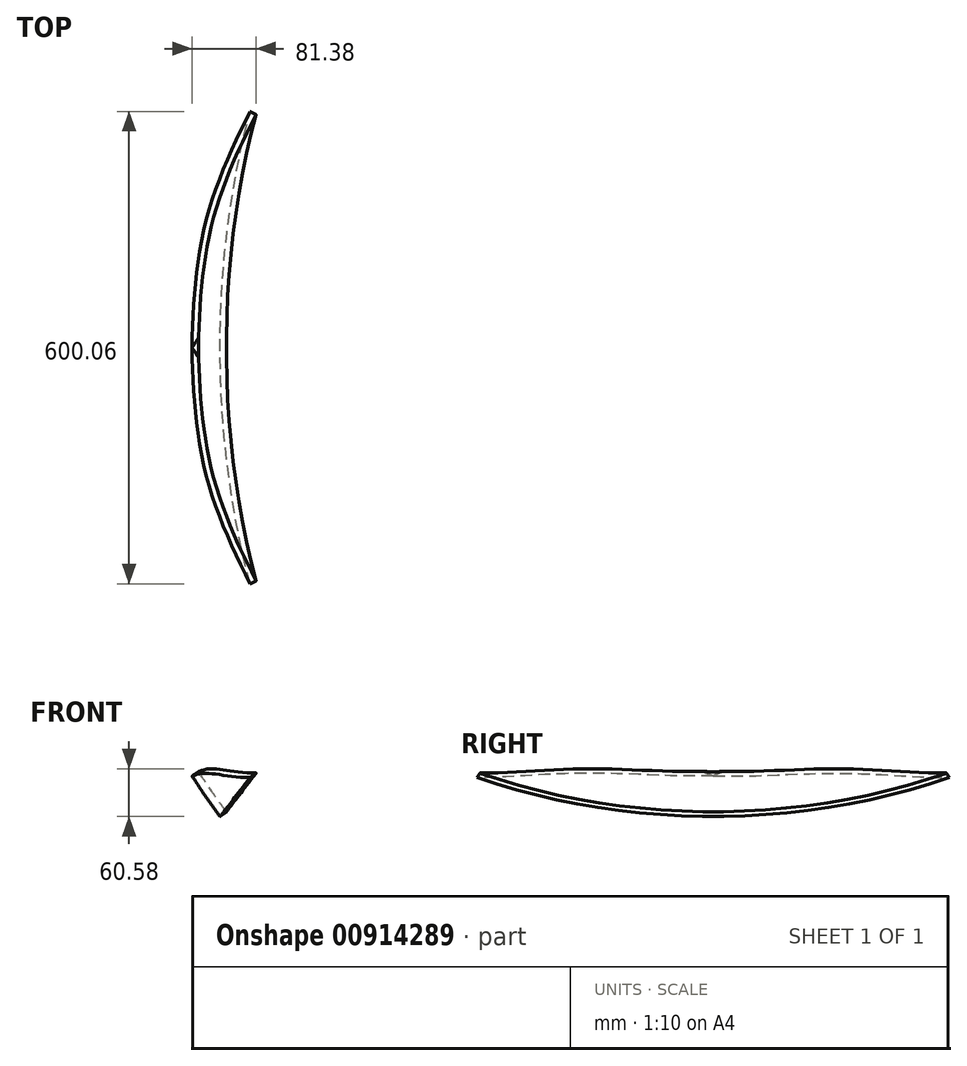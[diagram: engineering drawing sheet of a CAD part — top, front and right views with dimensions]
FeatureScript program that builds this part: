
annotation { "Feature Type Name" : "Feature", "Feature Type Description" : "" }
export const myFeature = defineFeature(function(context is Context, id is Id, definition is map)
    precondition{}
    {
        {
            var Q0;
            Q0=qCreatedBy(makeId("Front.planeOp"),FACE);
            var sketch = newSketch(context, id + "F0", { "sketchPlane" : qUnion([Q0])});
            skLineSegment(sketch, "E0", {"start": v(-634.43, -400) * mm, "end": v(-559, -400) * mm, "construction": true});
            skLineSegment(sketch, "E1", {"start": v(-559, -400) * mm, "end": v(-559, -500.02) * mm, "construction": true});
            skArc(sketch, "E2.trimOffspring", {"start": v(-634.43, -400) * mm, "mid": v(-617.16, -426.17) * mm, "end": v(-598.8, -451.59) * mm});
            skPoint(sketch, "E3.start.orphan", {"position": v(-750, 0) * mm});
            skPoint(sketch, "E4.orphan", {"position": v(0, -750) * mm});
            skLineSegment(sketch, "E5", {"start": v(-559, -500.02) * mm, "end": v(0, 0) * mm, "construction": true});
            skLineSegment(sketch, "E6", {"start": v(0, 0) * mm, "end": v(-634.43, -400) * mm, "construction": true});
            skPoint(sketch, "E7.end.orphan", {"position": v(-598.8, -451.59) * mm});
            skLineSegment(sketch, "E8", {"start": v(-598.8, -451.59) * mm, "end": v(-559, -400) * mm, "construction": true});
            skLineSegment(sketch, "E9", {"start": v(-559, -400) * mm, "end": v(-478.9, -489.54) * mm, "construction": true});
            skLineSegment(sketch, "E10", {"start": v(-478.9, -489.54) * mm, "end": v(-509.3, -455.56) * mm, "construction": true});
            skLineSegment(sketch, "E11", {"start": v(-559, -400) * mm, "end": v(-621.65, -329.96) * mm, "construction": true});
            skLineSegment(sketch, "E12", {"start": v(0, 0) * mm, "end": v(-559, -400) * mm, "construction": true});
            skArc(sketch, "E13", {"start": v(0, 26.26) * mm, "mid": v(-23.36, 12) * mm, "end": v(-21.36, -15.28) * mm, "construction": true});
            skLineSegment(sketch, "E14", {"start": v(0, 0) * mm, "end": v(0, 26.26) * mm, "construction": true});
            skLineSegment(sketch, "E15", {"start": v(-634.43, -400) * mm, "end": v(-625.97, -394.67) * mm});
            skLineSegment(sketch, "E16", {"start": v(-559, -500.02) * mm, "end": v(-551.55, -493.35) * mm});
            skArc(sketch, "E17", {"start": v(-625.97, -394.67) * mm, "mid": v(-608.93, -420.48) * mm, "end": v(-590.82, -445.57) * mm});
            skLineSegment(sketch, "E18", {"start": v(-598.8, -451.59) * mm, "end": v(-590.82, -445.57) * mm});
            skSolve(sketch);
        }
        {
            var Q0;
            Q0=sQuery(id+"F0.wireOp",EDGE,"E8");
            cPlane(context, id + "F1", {"entities" : qUnion([Q0]), "cplaneType" : CPlaneType.LINE_ANGLE, "offset" : 25 * mm, "angle" : 0 * degree, "width" : 150 * mm, "height" : 150 * mm});
        }
        {
            var Q0;
            Q0=qCreatedBy(id+"F1.planeOp",FACE);
            var sketch = newSketch(context, id + "F2", { "sketchPlane" : qUnion([Q0])});
            skArc(sketch, "E19", {"start": v(0, -723.34) * mm, "mid": v(153.25, -707.51) * mm, "end": v(300.03, -660.71) * mm});
            skSolve(sketch);
        }
        {
            var Q0;
            Q0=sQuery(id+"F0.wireOp",VERTEX,"E0.start");
            var Q1;
            Q1=sQuery(id+"F0.wireOp",VERTEX,"E7.end.orphan");
            var Q2;
            Q2=sQuery(id+"F2.wireOp",VERTEX,"E19.end");
            cPlane(context, id + "F3", {"entities" : qUnion([Q0, Q1, Q2]), "cplaneType" : CPlaneType.THREE_POINT, "offset" : 25 * mm, "width" : 150 * mm, "height" : 150 * mm});
        }
        {
            var Q0;
            Q0=qCreatedBy(id+"F3.planeOp",FACE);
            var sketch = newSketch(context, id + "F4", { "sketchPlane" : qUnion([Q0])});
            skFitSpline(sketch, "E20", {"points": [v(146.13, 31.35) * mm, v(-17.39, 23.69) * mm, v(-159.77, -12.29) * mm], "startDerivative": vector(-323.62, -9.9) * mm, "endDerivative": vector(-282.1, -74.81) * mm});
            skLineSegment(sketch, "E21", {"start": v(-159.77, -12.29) * mm, "end": v(-190.52, 25.33) * mm});
            skLineSegment(sketch, "E22", {"start": v(-190.52, 25.33) * mm, "end": v(-149.4, 94.45) * mm});
            skLineSegment(sketch, "E23", {"start": v(-149.4, 94.45) * mm, "end": v(148.54, 94.45) * mm});
            skLineSegment(sketch, "E24", {"start": v(148.54, 94.45) * mm, "end": v(146.13, 31.35) * mm});
            skSolve(sketch);
        }
        {
            var Q0;
            Q0=makeQuery(id+"F0.imprint","IMPRINT",FACE,{"disambiguationData":[TD([[makeQuery(id+"F0.imprint","IMPRINT",EDGE,{"derivedFrom":sQuery(id+"F0.wireOp",EDGE,"E2.trimOffspring")}),1.0]])]});
            var Q1;
            Q1=sQuery(id+"F2.wireOp",EDGE,"E19");
            sweep(context, id + "F5", {"profiles" : qUnion([Q0]), "path" : qUnion([Q1])});
        }
        {
            var Q0;
            Q0 = qSketchRegion(id + "F4", true);
            extrude(context, id + "F6", {"entities" : qUnion([Q0]), "operationType" : NewBodyOperationType.REMOVE, "endBound" : BoundingType.SYMMETRIC, "oppositeDirection" : true, "depth" : 38 * mm, "offsetDistance" : 25 * mm});
        }
        {
            var Q0;
            Q0=makeQuery(id+"F5.opSweep","SWEPT_BODY",BODY,{"disambiguationData":[OSD([sQuery(id+"F0.wireOp",EDGE,"E2.trimOffspring"),sQuery(id+"F0.wireOp",EDGE,"E15"),sQuery(id+"F0.wireOp",EDGE,"E17"),sQuery(id+"F0.wireOp",EDGE,"E18"),sQuery(id+"F2.wireOp",EDGE,"E19")])]});
            var Q1;
            Q1=makeQuery(id+"F5.opSweep","CAP_FACE",FACE,{"disambiguationData":[OSD([sQuery(id+"F0.wireOp",EDGE,"E2.trimOffspring"),sQuery(id+"F0.wireOp",EDGE,"E15"),sQuery(id+"F0.wireOp",EDGE,"E17"),sQuery(id+"F0.wireOp",EDGE,"E18"),sQuery(id+"F2.wireOp",VERTEX,"E19.start")])],"isStart":true});
            mirror(context, id + "F7", {"operationType" : NewBodyOperationType.ADD, "entities" : qUnion([Q0]), "mirrorPlane" : qUnion([Q1])});
        }
    });
